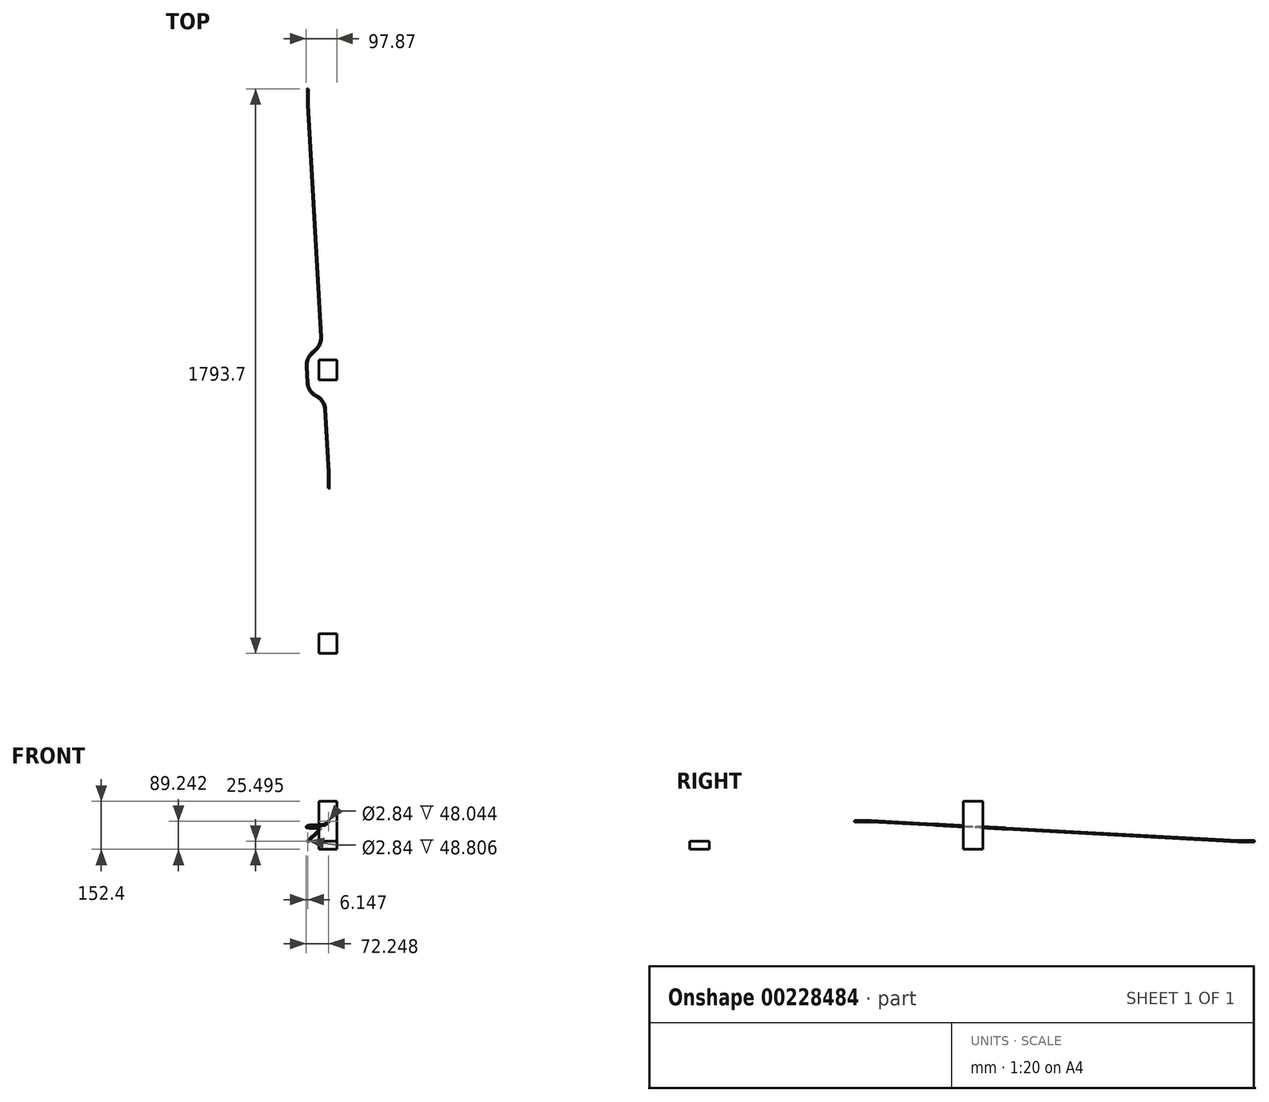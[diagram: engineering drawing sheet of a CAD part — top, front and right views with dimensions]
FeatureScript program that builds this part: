
annotation { "Feature Type Name" : "Feature", "Feature Type Description" : "" }
export const myFeature = defineFeature(function(context is Context, id is Id, definition is map)
    precondition{}
    {
        {
            var Q0;
            Q0=qCreatedBy(makeId("Top.planeOp"),FACE);
            var sketch = newSketch(context, id + "F0", { "sketchPlane" : qUnion([Q0])});
            skLineSegment(sketch, "E0", {"start": v(0, 0) * mm, "end": v(2.87, 0) * mm});
            skLineSegment(sketch, "E1", {"start": v(2.87, 0) * mm, "end": v(2.87, 58) * mm});
            skLineSegment(sketch, "E2", {"start": v(2.87, 58) * mm, "end": v(28.27, 58) * mm});
            skLineSegment(sketch, "E3", {"start": v(0, 0) * mm, "end": v(-63.23, 0) * mm});
            skLineSegment(sketch, "E4", {"start": v(-63.23, 0) * mm, "end": v(-63.23, 1327.37) * mm});
            skLineSegment(sketch, "E5", {"start": v(-63.23, 1327.37) * mm, "end": v(-37.83, 1327.37) * mm});
            skSolve(sketch);
        }
        {
            var Q0;
            Q0=sQuery(id+"F0.wireOp",EDGE,"E5");
            cPlane(context, id + "F1", {"entities" : qUnion([Q0]), "cplaneType" : CPlaneType.LINE_ANGLE, "offset" : 25.4 * mm, "angle" : 0 * degree, "width" : 152.4 * mm, "height" : 152.4 * mm});
        }
        {
            var Q0;
            Q0=sQuery(id+"F0.wireOp",EDGE,"E2");
            cPlane(context, id + "F2", {"entities" : qUnion([Q0]), "cplaneType" : CPlaneType.LINE_ANGLE, "offset" : 25.4 * mm, "angle" : 0 * degree, "width" : 152.4 * mm, "height" : 152.4 * mm});
        }
        {
            var Q0;
            Q0=qCreatedBy(id+"F2.planeOp",FACE);
            var sketch = newSketch(context, id + "F3", { "sketchPlane" : qUnion([Q0])});
            skLineSegment(sketch, "E6", {"start": v(-2.87, 0) * mm, "end": v(-2.87, 861.48) * mm});
            skSolve(sketch);
        }
        {
            var Q0;
            Q0=qCreatedBy(id+"F1.planeOp",FACE);
            var sketch = newSketch(context, id + "F4", { "sketchPlane" : qUnion([Q0])});
            skLineSegment(sketch, "E7", {"start": v(63.23, 0) * mm, "end": v(63.23, 797.74) * mm});
            skSolve(sketch);
        }
        {
            var Q0;
            Q0=sQuery(id+"F4.wireOp",EDGE,"E7");
            cPlane(context, id + "F5", {"entities" : qUnion([Q0]), "cplaneType" : CPlaneType.LINE_ANGLE, "offset" : 25.4 * mm, "angle" : 90 * degree, "width" : 152.4 * mm, "height" : 152.4 * mm});
        }
        {
            var Q0;
            Q0=sQuery(id+"F4.wireOp",EDGE,"E7");
            cPlane(context, id + "F6", {"entities" : qUnion([Q0]), "cplaneType" : CPlaneType.LINE_ANGLE, "offset" : 25.4 * mm, "angle" : 0 * degree, "width" : 152.4 * mm, "height" : 152.4 * mm});
        }
        {
            var Q0;
            Q0=sQuery(id+"F3.wireOp",EDGE,"E6");
            cPlane(context, id + "F7", {"entities" : qUnion([Q0]), "cplaneType" : CPlaneType.LINE_ANGLE, "offset" : 25.4 * mm, "angle" : 0 * degree, "width" : 152.4 * mm, "height" : 152.4 * mm});
        }
        {
            var Q0;
            Q0=sQuery(id+"F3.wireOp",EDGE,"E6");
            cPlane(context, id + "F8", {"entities" : qUnion([Q0]), "cplaneType" : CPlaneType.LINE_ANGLE, "offset" : 25.4 * mm, "angle" : 90 * degree, "width" : 152.4 * mm, "height" : 152.4 * mm});
        }
        {
            var Q0;
            Q0=qCreatedBy(id+"F8.planeOp",FACE);
            var sketch = newSketch(context, id + "F9", { "sketchPlane" : qUnion([Q0])});
            skCircle(sketch, "E8", {"center": v(-2.87, 861.48) * mm, "radius": 2.18 * mm});
            skSolve(sketch);
        }
        {
            var Q0;
            Q0=qCreatedBy(id+"F5.planeOp",FACE);
            var sketch = newSketch(context, id + "F10", { "sketchPlane" : qUnion([Q0])});
            skCircle(sketch, "E9", {"center": v(63.23, 797.74) * mm, "radius": 2.18 * mm});
            skSolve(sketch);
        }
        {
            var Q0;
            Q0=qCreatedBy(id+"F6.planeOp",FACE);
            var sketch = newSketch(context, id + "F11", { "sketchPlane" : qUnion([Q0])});
            skLineSegment(sketch, "E10", {"start": v(1327.37, 797.74) * mm, "end": v(1276.57, 797.74) * mm});
            skSolve(sketch);
        }
        {
            var Q0;
            Q0=qCreatedBy(id+"F7.planeOp",FACE);
            var sketch = newSketch(context, id + "F12", { "sketchPlane" : qUnion([Q0])});
            skLineSegment(sketch, "E11", {"start": v(58, 861.48) * mm, "end": v(108.8, 861.48) * mm});
            skSolve(sketch);
        }
        {
            var Q0;
            Q0=sQuery(id+"F12.wireOp",VERTEX,"E11.start");
            var Q1;
            Q1=sQuery(id+"F12.wireOp",VERTEX,"E11.end");
            var Q2;
            Q2=sQuery(id+"F11.wireOp",VERTEX,"E10.end");
            cPlane(context, id + "F13", {"entities" : qUnion([Q0, Q1, Q2]), "cplaneType" : CPlaneType.THREE_POINT, "offset" : 25.4 * mm, "width" : 152.4 * mm, "height" : 152.4 * mm});
        }
        {
            var Q0;
            Q0=qCreatedBy(id+"F13.planeOp",FACE);
            var sketch = newSketch(context, id + "F14", { "sketchPlane" : qUnion([Q0])});
            skLineSegment(sketch, "E12", {"start": v(599.92, -110.8) * mm, "end": v(508.25, -1276.57) * mm});
            skLineSegment(sketch, "E13", {"start": v(600.08, -106.81) * mm, "end": v(600.08, -58) * mm});
            skPoint(sketch, "E14.visualSharp", {"position": v(600.08, -108.8) * mm});
            skArc(sketch, "E14.filletArc", {"start": v(599.92, -110.8) * mm, "mid": v(600.04, -108.8) * mm, "end": v(600.08, -106.81) * mm});
            skSolve(sketch);
        }
        {
            var Q0;
            Q0=sQuery(id+"F14.wireOp",EDGE,"E12");
            var Q1;
            Q1=sQuery(id+"F11.wireOp",EDGE,"E10");
            cPlane(context, id + "F15", {"entities" : qUnion([Q0, Q1]), "cplaneType" : CPlaneType.LINE_ANGLE, "offset" : 25.4 * mm, "angle" : 0 * degree, "width" : 152.4 * mm, "height" : 152.4 * mm});
        }
        {
            var Q0;
            Q0=qCreatedBy(id+"F15.planeOp",FACE);
            var sketch = newSketch(context, id + "F16", { "sketchPlane" : qUnion([Q0])});
            skLineSegment(sketch, "E15", {"start": v(508.25, 1327.37) * mm, "end": v(508.25, 1278.56) * mm});
            skLineSegment(sketch, "E16", {"start": v(508.4, 1274.58) * mm, "end": v(599.92, 110.8) * mm});
            skPoint(sketch, "E17.visualSharp", {"position": v(508.25, 1276.57) * mm});
            skArc(sketch, "E17.filletArc", {"start": v(508.25, 1278.56) * mm, "mid": v(508.29, 1276.57) * mm, "end": v(508.4, 1274.58) * mm});
            skSolve(sketch);
        }
        {
            var Q0;
            Q0=makeQuery(id+"F10.imprint","IMPRINT",FACE,{"disambiguationData":[TD([[makeQuery(id+"F10.imprint","IMPRINT",EDGE,{"derivedFrom":sQuery(id+"F10.wireOp",EDGE,"E9")}),1.0]])]});
            var Q1;
            Q1=sQuery(id+"F16.wireOp",EDGE,"E15");
            var Q2;
            Q2=sQuery(id+"F16.wireOp",EDGE,"E17.filletArc");
            var Q3;
            Q3=sQuery(id+"F16.wireOp",EDGE,"E16");
            var Q4;
            Q4=sQuery(id+"F14.wireOp",EDGE,"E14.filletArc");
            var Q5;
            Q5=sQuery(id+"F14.wireOp",EDGE,"E13");
            sweep(context, id + "F17", {"profiles" : qUnion([Q0]), "path" : qUnion([Q1, Q2, Q3, Q4, Q5])});
        }
        {
            var Q0;
            Q0=makeQuery(id+"F17.opSweep","CAP_FACE",FACE,{"disambiguationData":[OSD([sQuery(id+"F10.wireOp",EDGE,"E9"),sQuery(id+"F14.wireOp",VERTEX,"E13.end")])],"isStart":false});
            shell(context, id + "F18", {"entities" : qUnion([Q0]), "thickness" : 0.76 * mm});
        }
        {
            var Q0;
            Q0=qCreatedBy(makeId("Top.planeOp"),FACE);
            var sketch = newSketch(context, id + "F19", { "sketchPlane" : qUnion([Q0])});
            skLineSegment(sketch, "E18", {"start": v(0, 0) * mm, "end": v(-27.9, 0) * mm});
            skLineSegment(sketch, "E19", {"start": v(-27.9, 0) * mm, "end": v(-27.9, -466.33) * mm});
            skLineSegment(sketch, "E20", {"start": v(-27.9, -466.33) * mm, "end": v(-2.5, -466.33) * mm});
            skLineSegment(sketch, "E21", {"start": v(0, 0) * mm, "end": v(28.49, 0) * mm});
            skLineSegment(sketch, "E22", {"start": v(28.49, 0) * mm, "end": v(28.49, -403.6) * mm});
            skLineSegment(sketch, "E23", {"start": v(28.49, -403.6) * mm, "end": v(53.89, -403.6) * mm});
            skSolve(sketch);
        }
        {
            var Q0;
            Q0=sQuery(id+"F19.wireOp",EDGE,"E20");
            cPlane(context, id + "F20", {"entities" : qUnion([Q0]), "cplaneType" : CPlaneType.LINE_ANGLE, "offset" : 25.4 * mm, "angle" : 0 * degree, "width" : 152.4 * mm, "height" : 152.4 * mm});
        }
        {
            var Q0;
            Q0=sQuery(id+"F19.wireOp",EDGE,"E23");
            cPlane(context, id + "F21", {"entities" : qUnion([Q0]), "cplaneType" : CPlaneType.LINE_ANGLE, "offset" : 25.4 * mm, "angle" : 0 * degree, "width" : 152.4 * mm, "height" : 152.4 * mm});
        }
        {
            var Q0;
            Q0=qCreatedBy(id+"F20.planeOp",FACE);
            var sketch = newSketch(context, id + "F22", { "sketchPlane" : qUnion([Q0])});
            skLineSegment(sketch, "E24", {"start": v(27.9, 0) * mm, "end": v(27.9, 772.24) * mm});
            skLineSegment(sketch, "E25", {"start": v(27.9, 772.24) * mm, "end": v(2.5, 772.24) * mm});
            skSolve(sketch);
        }
        {
            var Q0;
            Q0=qCreatedBy(id+"F21.planeOp",FACE);
            var sketch = newSketch(context, id + "F23", { "sketchPlane" : qUnion([Q0])});
            skLineSegment(sketch, "E26", {"start": v(-28.49, 0) * mm, "end": v(-28.49, 772.24) * mm});
            skSolve(sketch);
        }
        {
            var Q0;
            Q0=sQuery(id+"F22.wireOp",EDGE,"E25");
            cPlane(context, id + "F24", {"entities" : qUnion([Q0]), "cplaneType" : CPlaneType.LINE_ANGLE, "offset" : 25.4 * mm, "angle" : 90 * degree, "width" : 152.4 * mm, "height" : 152.4 * mm});
        }
        {
            var Q0;
            Q0=qCreatedBy(id+"F24.planeOp",FACE);
            var sketch = newSketch(context, id + "F25", { "sketchPlane" : qUnion([Q0])});
            skLineSegment(sketch, "E27.bottom", {"start": v(-27.9, -466.33) * mm, "end": v(28.49, -466.33) * mm});
            skLineSegment(sketch, "E27.top", {"start": v(-27.9, -403.6) * mm, "end": v(28.49, -403.6) * mm});
            skLineSegment(sketch, "E27.left", {"start": v(-27.9, -466.33) * mm, "end": v(-27.9, -403.6) * mm});
            skLineSegment(sketch, "E27.right", {"start": v(28.49, -466.33) * mm, "end": v(28.49, -403.6) * mm});
            skSolve(sketch);
        }
        {
            var Q0;
            Q0 = qSketchRegion(id + "F25", true);
            extrude(context, id + "F26", {"entities" : qUnion([Q0]), "depth" : 25.4 * mm});
        }
        {
            var Q0;
            Q0=qCreatedBy(makeId("Top.planeOp"),FACE);
            var sketch = newSketch(context, id + "F27", { "sketchPlane" : qUnion([Q0])});
            skLineSegment(sketch, "E28", {"start": v(0, 0) * mm, "end": v(28.44, 0) * mm});
            skLineSegment(sketch, "E29", {"start": v(28.44, 0) * mm, "end": v(28.44, 465.82) * mm});
            skLineSegment(sketch, "E30", {"start": v(28.44, 465.82) * mm, "end": v(3.04, 465.82) * mm});
            skLineSegment(sketch, "E31", {"start": v(0, 0) * mm, "end": v(-27.96, 0) * mm});
            skLineSegment(sketch, "E32", {"start": v(-27.96, 0) * mm, "end": v(-27.96, 403.08) * mm});
            skLineSegment(sketch, "E33", {"start": v(-27.96, 403.08) * mm, "end": v(-53.36, 403.08) * mm});
            skSolve(sketch);
        }
        {
            var Q0;
            Q0=sQuery(id+"F27.wireOp",EDGE,"E30");
            cPlane(context, id + "F28", {"entities" : qUnion([Q0]), "cplaneType" : CPlaneType.LINE_ANGLE, "offset" : 25.4 * mm, "angle" : 0 * degree, "width" : 152.4 * mm, "height" : 152.4 * mm});
        }
        {
            var Q0;
            Q0=sQuery(id+"F27.wireOp",EDGE,"E33");
            cPlane(context, id + "F29", {"entities" : qUnion([Q0]), "cplaneType" : CPlaneType.LINE_ANGLE, "offset" : 25.4 * mm, "angle" : 0 * degree, "width" : 152.4 * mm, "height" : 152.4 * mm});
        }
        {
            var Q0;
            Q0=qCreatedBy(id+"F28.planeOp",FACE);
            var sketch = newSketch(context, id + "F30", { "sketchPlane" : qUnion([Q0])});
            skLineSegment(sketch, "E34", {"start": v(28.44, 0) * mm, "end": v(28.44, 772.24) * mm});
            skLineSegment(sketch, "E35", {"start": v(28.44, 772.24) * mm, "end": v(3.04, 772.24) * mm});
            skSolve(sketch);
        }
        {
            var Q0;
            Q0=qCreatedBy(id+"F29.planeOp",FACE);
            var sketch = newSketch(context, id + "F31", { "sketchPlane" : qUnion([Q0])});
            skLineSegment(sketch, "E36", {"start": v(-27.96, 0) * mm, "end": v(-27.96, 772.24) * mm});
            skSolve(sketch);
        }
        {
            var Q0;
            Q0=sQuery(id+"F30.wireOp",EDGE,"E35");
            cPlane(context, id + "F32", {"entities" : qUnion([Q0]), "cplaneType" : CPlaneType.LINE_ANGLE, "offset" : 25.4 * mm, "angle" : 90 * degree, "width" : 152.4 * mm, "height" : 152.4 * mm});
        }
        {
            var Q0;
            Q0=qCreatedBy(id+"F32.planeOp",FACE);
            var sketch = newSketch(context, id + "F33", { "sketchPlane" : qUnion([Q0])});
            skLineSegment(sketch, "E37.bottom", {"start": v(28.44, 465.82) * mm, "end": v(-27.96, 465.82) * mm});
            skLineSegment(sketch, "E37.top", {"start": v(28.44, 403.08) * mm, "end": v(-27.96, 403.08) * mm});
            skLineSegment(sketch, "E37.left", {"start": v(28.44, 465.82) * mm, "end": v(28.44, 403.08) * mm});
            skLineSegment(sketch, "E37.right", {"start": v(-27.96, 465.82) * mm, "end": v(-27.96, 403.08) * mm});
            skSolve(sketch);
        }
        {
            var Q0;
            Q0 = qSketchRegion(id + "F33", true);
            extrude(context, id + "F34", {"entities" : qUnion([Q0]), "depth" : 152.4 * mm});
        }
        {
            var Q0;
            Q0=makeQuery(id+"F17.opSweep","SWEPT_BODY",BODY,{"disambiguationData":[OSD([sQuery(id+"F10.wireOp",EDGE,"E9"),sQuery(id+"F14.wireOp",EDGE,"E13")])]});
            deleteBodies(context, id + "F35", {"entities" : qUnion([Q0])});
        }
        {
            var Q0;
            Q0=sQuery(id+"F16.wireOp",EDGE,"E16");
            cPlane(context, id + "F36", {"entities" : qUnion([Q0]), "cplaneType" : CPlaneType.LINE_ANGLE, "offset" : 25.4 * mm, "angle" : 0 * degree, "width" : 152.4 * mm, "height" : 152.4 * mm});
        }
        {
            var Q0;
            Q0=qCreatedBy(id+"F36.planeOp",FACE);
            var sketch = newSketch(context, id + "F37", { "sketchPlane" : qUnion([Q0])});
            skLineSegment(sketch, "E38", {"start": v(-10.14, -291.91) * mm, "end": v(-20.18, -469.43) * mm});
            skLineSegment(sketch, "E39", {"start": v(-20.18, -469.43) * mm, "end": v(-51.7, -438.97) * mm});
            skLineSegment(sketch, "E40", {"start": v(-67.11, -399.58) * mm, "end": v(-64.14, -346.93) * mm});
            skLineSegment(sketch, "E41", {"start": v(-35.35, -303.98) * mm, "end": v(-10.14, -291.91) * mm});
            skPoint(sketch, "E42.visualSharp", {"position": v(-62.44, -316.94) * mm});
            skArc(sketch, "E42.filletArc", {"start": v(-35.35, -303.98) * mm, "mid": v(-55.62, -321.52) * mm, "end": v(-64.14, -346.93) * mm});
            skPoint(sketch, "E43.visualSharp", {"position": v(-68.42, -422.8) * mm});
            skArc(sketch, "E43.filletArc", {"start": v(-67.11, -399.58) * mm, "mid": v(-63.7, -420.96) * mm, "end": v(-51.7, -438.97) * mm});
            skLineSegment(sketch, "E44", {"start": v(-64.14, -346.93) * mm, "end": v(-13.42, -349.8) * mm});
            skLineSegment(sketch, "E45", {"start": v(-10.14, -291.91) * mm, "end": v(2.76, -63.68) * mm});
            skSolve(sketch);
        }
        {
            var Q0;
            Q0=sQuery(id+"F37.wireOp",EDGE,"E41");
            var Q1;
            Q1=sQuery(id+"F37.wireOp",EDGE,"E45");
            cPlane(context, id + "F38", {"entities" : qUnion([Q0, Q1]), "cplaneType" : CPlaneType.LINE_ANGLE, "offset" : 25.4 * mm, "angle" : 0 * degree, "width" : 152.4 * mm, "height" : 152.4 * mm});
        }
        {
            var Q0;
            Q0=qCreatedBy(id+"F38.planeOp",FACE);
            var sketch = newSketch(context, id + "F39", { "sketchPlane" : qUnion([Q0])});
            skLineSegment(sketch, "E46", {"start": v(-8.45, -261.98) * mm, "end": v(2.76, -63.68) * mm});
            skPoint(sketch, "E47.visualSharp", {"position": v(-10.14, -291.91) * mm});
            skArc(sketch, "E47.filletArc", {"start": v(-35.35, -303.98) * mm, "mid": v(-16.4, -286.5) * mm, "end": v(-8.45, -261.98) * mm});
            skSolve(sketch);
        }
        {
            var Q0;
            Q0=sQuery(id+"F37.wireOp",EDGE,"E39");
            var Q1;
            Q1=sQuery(id+"F16.wireOp",EDGE,"E16");
            cPlane(context, id + "F40", {"entities" : qUnion([Q0, Q1]), "cplaneType" : CPlaneType.LINE_ANGLE, "offset" : 25.4 * mm, "angle" : 0 * degree, "width" : 152.4 * mm, "height" : 152.4 * mm});
        }
        {
            var Q0;
            Q0=qCreatedBy(id+"F40.planeOp",FACE);
            var sketch = newSketch(context, id + "F41", { "sketchPlane" : qUnion([Q0])});
            skLineSegment(sketch, "E48", {"start": v(-51.7, 438.97) * mm, "end": v(-36.9, 453.26) * mm});
            skLineSegment(sketch, "E49", {"start": v(-21.5, 492.66) * mm, "end": v(-63.12, 1229.2) * mm});
            skPoint(sketch, "E50.visualSharp", {"position": v(-20.18, 469.43) * mm});
            skArc(sketch, "E50.filletArc", {"start": v(-36.9, 453.26) * mm, "mid": v(-24.9, 471.28) * mm, "end": v(-21.5, 492.66) * mm});
            skSolve(sketch);
        }
        {
            var Q0;
            Q0=makeQuery(id+"F9.imprint","IMPRINT",FACE,{"disambiguationData":[TD([[makeQuery(id+"F9.imprint","IMPRINT",EDGE,{"derivedFrom":sQuery(id+"F9.wireOp",EDGE,"E8")}),1.0]])]});
            var Q1;
            Q1=sQuery(id+"F14.wireOp",EDGE,"E13");
            var Q2;
            Q2=sQuery(id+"F14.wireOp",EDGE,"E14.filletArc");
            var Q3;
            Q3=sQuery(id+"F39.wireOp",EDGE,"E46");
            var Q4;
            Q4=sQuery(id+"F39.wireOp",EDGE,"E47.filletArc");
            var Q5;
            Q5=sQuery(id+"F37.wireOp",EDGE,"E42.filletArc");
            var Q6;
            Q6=sQuery(id+"F37.wireOp",EDGE,"E40");
            var Q7;
            Q7=sQuery(id+"F37.wireOp",EDGE,"E43.filletArc");
            var Q8;
            Q8=sQuery(id+"F41.wireOp",EDGE,"E48");
            var Q9;
            Q9=sQuery(id+"F41.wireOp",EDGE,"E50.filletArc");
            var Q10;
            Q10=sQuery(id+"F41.wireOp",EDGE,"E49");
            var Q11;
            Q11=sQuery(id+"F16.wireOp",EDGE,"E17.filletArc");
            var Q12;
            Q12=sQuery(id+"F16.wireOp",EDGE,"E15");
            sweep(context, id + "F42", {"profiles" : qUnion([Q0]), "path" : qUnion([Q1, Q2, Q3, Q4, Q5, Q6, Q7, Q8, Q9, Q10, Q11, Q12])});
        }
        {
            var Q0;
            Q0=makeQuery(id+"F42.opSweep","CAP_FACE",FACE,{"disambiguationData":[OSD([sQuery(id+"F9.wireOp",EDGE,"E8"),sQuery(id+"F16.wireOp",VERTEX,"E15.start")])],"isStart":false});
            shell(context, id + "F43", {"entities" : qUnion([Q0]), "thickness" : 0.76 * mm});
        }
        {
            var Q0;
            Q0=makeQuery(id+"F34.opExtrude","SWEPT_BODY",BODY,{"disambiguationData":[OSD([sQuery(id+"F33.wireOp",EDGE,"E37.bottom"),sQuery(id+"F33.wireOp",EDGE,"E37.top"),sQuery(id+"F33.wireOp",EDGE,"E37.left"),sQuery(id+"F33.wireOp",EDGE,"E37.right")])]});
            transform(context, id + "F44", {"entities" : qUnion([Q0]), "transformType" : TransformType.TRANSLATION_3D, "dx" : 0 * mm, "dy" : 0 * mm, "dz" : 0 * mm, "makeCopy" : true});
        }
        {
            var Q0;
            Q0=makeQuery(id+"F34.opExtrude","SWEPT_BODY",BODY,{"disambiguationData":[OSD([sQuery(id+"F33.wireOp",EDGE,"E37.bottom"),sQuery(id+"F33.wireOp",EDGE,"E37.top"),sQuery(id+"F33.wireOp",EDGE,"E37.left"),sQuery(id+"F33.wireOp",EDGE,"E37.right")])]});
            transform(context, id + "F45", {"entities" : qUnion([Q0]), "transformType" : TransformType.TRANSLATION_3D, "dx" : 0 * mm, "dy" : 0 * mm, "dz" : 0 * mm, "makeCopy" : true});
        }
    });
